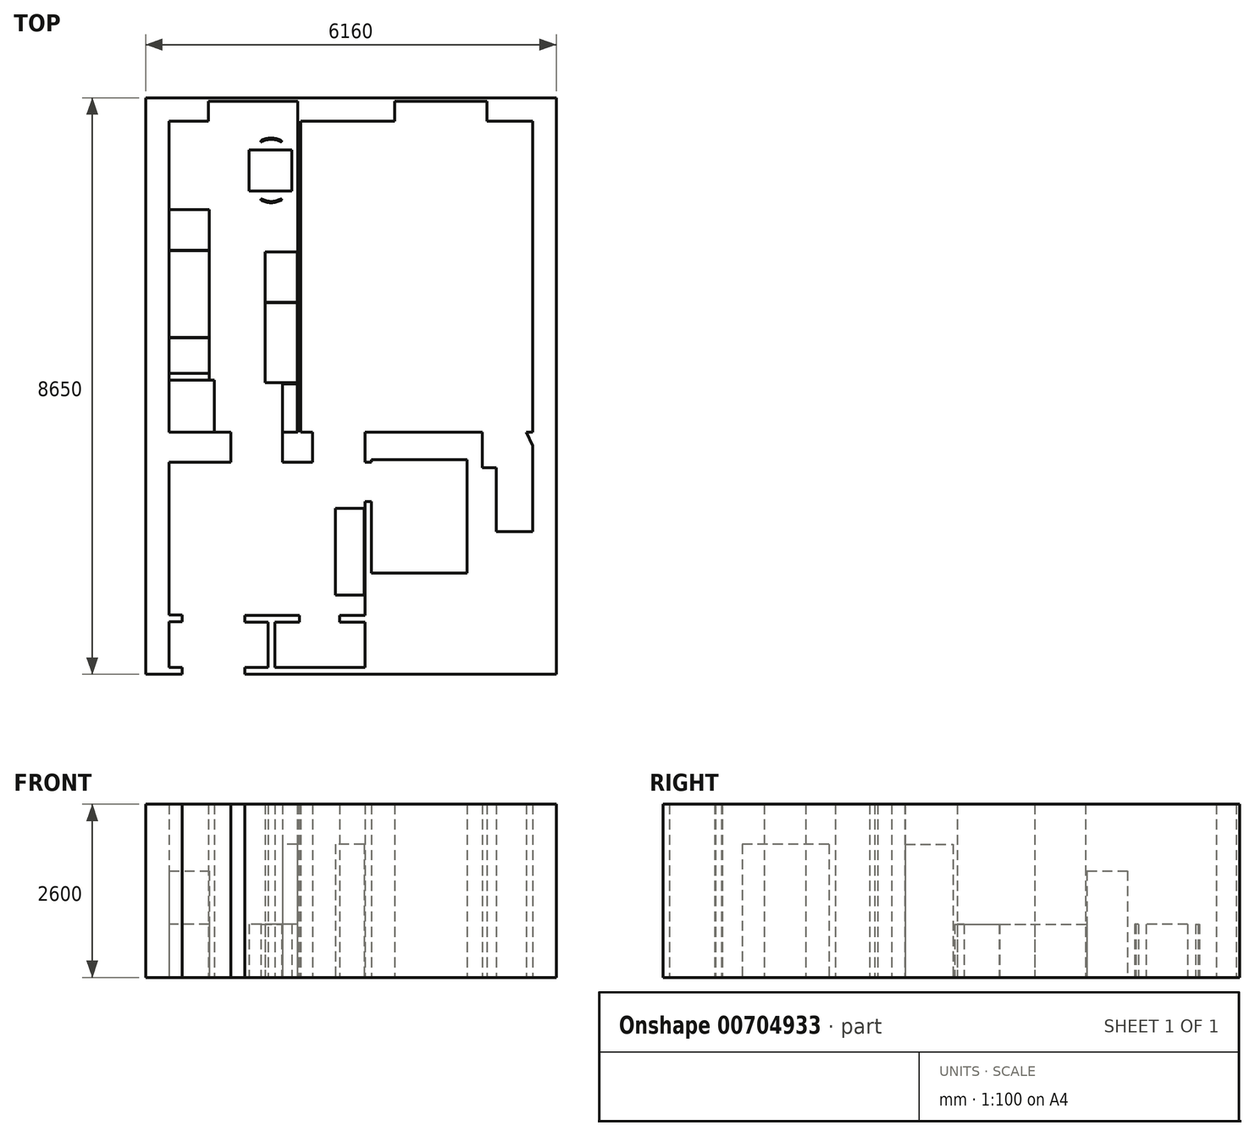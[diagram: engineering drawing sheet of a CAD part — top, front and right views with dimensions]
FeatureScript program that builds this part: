
annotation { "Feature Type Name" : "Feature", "Feature Type Description" : "" }
export const myFeature = defineFeature(function(context is Context, id is Id, definition is map)
    precondition{}
    {
        {
            var Q0;
            Q0=qCreatedBy(makeId("Top.planeOp"),FACE);
            var sketch = newSketch(context, id + "F0", { "sketchPlane" : qUnion([Q0])});
            skLineSegment(sketch, "E0.bottom", {"start": v(0, 5020) * mm, "end": v(-6160, 5020) * mm});
            skLineSegment(sketch, "E0.left", {"start": v(0, 5020) * mm, "end": v(0, -3630) * mm});
            skLineSegment(sketch, "E0.right", {"start": v(-6160, 5020) * mm, "end": v(-6160, -3630) * mm});
            skPoint(sketch, "E0.middle", {"position": v(-3830, 0) * mm});
            skLineSegment(sketch, "E1.bottom", {"start": v(-350, 4670) * mm, "end": v(-1040, 4670) * mm});
            skLineSegment(sketch, "E1.top", {"start": v(-350, 0) * mm, "end": v(-450, 0) * mm});
            skLineSegment(sketch, "E1.left", {"start": v(-350, 4670) * mm, "end": v(-350, 0) * mm});
            skLineSegment(sketch, "E1.right", {"start": v(-3830, 4670) * mm, "end": v(-3830, 0) * mm});
            skLineSegment(sketch, "E2.top", {"start": v(-1040, 4970) * mm, "end": v(-2420, 4970) * mm});
            skLineSegment(sketch, "E2.left", {"start": v(-1040, 4670) * mm, "end": v(-1040, 4970) * mm});
            skLineSegment(sketch, "E2.right", {"start": v(-2420, 4670) * mm, "end": v(-2420, 4970) * mm});
            skLineSegment(sketch, "E3.trimOffspring", {"start": v(-2420, 4670) * mm, "end": v(-3830, 4670) * mm});
            skLineSegment(sketch, "E4", {"start": v(-350, -200) * mm, "end": v(-350, -1490) * mm});
            skLineSegment(sketch, "E5", {"start": v(-350, -1490) * mm, "end": v(-900, -1490) * mm});
            skLineSegment(sketch, "E6", {"start": v(-900, -1490) * mm, "end": v(-900, -530) * mm});
            skLineSegment(sketch, "E7", {"start": v(-900, -530) * mm, "end": v(-1110, -530) * mm});
            skLineSegment(sketch, "E8", {"start": v(-1110, -530) * mm, "end": v(-1110, 0) * mm});
            skLineSegment(sketch, "E9", {"start": v(-450, 0) * mm, "end": v(-350, -200) * mm});
            skLineSegment(sketch, "E10.trimOffspring", {"start": v(-1110, 0) * mm, "end": v(-2870, 0) * mm});
            skLineSegment(sketch, "E11", {"start": v(-3655, 0) * mm, "end": v(-3655, -450) * mm});
            skLineSegment(sketch, "E12", {"start": v(-3655, -450) * mm, "end": v(-4105, -450) * mm});
            skLineSegment(sketch, "E13", {"start": v(-4105, -450) * mm, "end": v(-4105, 0) * mm});
            skLineSegment(sketch, "E14", {"start": v(-4105, 0) * mm, "end": v(-3880, 0) * mm});
            skLineSegment(sketch, "E15", {"start": v(-3880, 0) * mm, "end": v(-3880, 4670) * mm});
            skLineSegment(sketch, "E16", {"start": v(-3880, 4670) * mm, "end": v(-3880, 4970) * mm});
            skLineSegment(sketch, "E17", {"start": v(-3880, 4970) * mm, "end": v(-5220, 4970) * mm});
            skLineSegment(sketch, "E18", {"start": v(-5220, 4970) * mm, "end": v(-5220, 4670) * mm});
            skLineSegment(sketch, "E19", {"start": v(-5220, 4670) * mm, "end": v(-5810, 4670) * mm});
            skLineSegment(sketch, "E20", {"start": v(-5810, 4670) * mm, "end": v(-5810, 0) * mm});
            skLineSegment(sketch, "E21", {"start": v(-5810, 0) * mm, "end": v(-4880, 0) * mm});
            skLineSegment(sketch, "E22", {"start": v(-4880, 0) * mm, "end": v(-4880, -450) * mm});
            skLineSegment(sketch, "E23", {"start": v(-4880, -450) * mm, "end": v(-5810, -450) * mm});
            skLineSegment(sketch, "E24", {"start": v(-5810, -450) * mm, "end": v(-5810, -2740) * mm});
            skLineSegment(sketch, "E25", {"start": v(-2870, -450) * mm, "end": v(-2770, -450) * mm});
            skLineSegment(sketch, "E26", {"start": v(-2770, -450) * mm, "end": v(-2770, -410) * mm});
            skLineSegment(sketch, "E27", {"start": v(-2770, -410) * mm, "end": v(-1340, -410) * mm});
            skLineSegment(sketch, "E28", {"start": v(-1340, -410) * mm, "end": v(-1340, -2110) * mm});
            skLineSegment(sketch, "E29.trimOffspring", {"start": v(-3655, 0) * mm, "end": v(-3830, 0) * mm});
            skLineSegment(sketch, "E30", {"start": v(-5810, -2740) * mm, "end": v(-5610, -2740) * mm});
            skLineSegment(sketch, "E31", {"start": v(-5610, -2740) * mm, "end": v(-5610, -2840) * mm});
            skLineSegment(sketch, "E32", {"start": v(-5610, -2840) * mm, "end": v(-5810, -2840) * mm});
            skLineSegment(sketch, "E33", {"start": v(-5810, -2840) * mm, "end": v(-5810, -3530) * mm});
            skLineSegment(sketch, "E34", {"start": v(-5810, -3530) * mm, "end": v(-5610, -3530) * mm});
            skLineSegment(sketch, "E35", {"start": v(-2870, 0) * mm, "end": v(-2870, -450) * mm});
            skLineSegment(sketch, "E36", {"start": v(-1340, -2110) * mm, "end": v(-2770, -2110) * mm});
            skLineSegment(sketch, "E37", {"start": v(-2770, -2110) * mm, "end": v(-2770, -1040) * mm});
            skLineSegment(sketch, "E38", {"start": v(-2770, -1040) * mm, "end": v(-2870, -1040) * mm});
            skLineSegment(sketch, "E39", {"start": v(-2870, -1040) * mm, "end": v(-2870, -2750) * mm});
            skLineSegment(sketch, "E40.bottom", {"start": v(-2880, -1140) * mm, "end": v(-3310, -1140) * mm});
            skLineSegment(sketch, "E40.top", {"start": v(-2880, -2440) * mm, "end": v(-3310, -2440) * mm});
            skLineSegment(sketch, "E40.left", {"start": v(-2880, -1140) * mm, "end": v(-2880, -2440) * mm});
            skLineSegment(sketch, "E40.right", {"start": v(-3310, -1140) * mm, "end": v(-3310, -2440) * mm});
            skLineSegment(sketch, "E41", {"start": v(-2870, -2750) * mm, "end": v(-3250, -2750) * mm});
            skLineSegment(sketch, "E42", {"start": v(-3250, -2750) * mm, "end": v(-3250, -2850) * mm});
            skLineSegment(sketch, "E43", {"start": v(-3250, -2850) * mm, "end": v(-2870, -2850) * mm});
            skLineSegment(sketch, "E44", {"start": v(-2870, -2850) * mm, "end": v(-2870, -3530) * mm});
            skLineSegment(sketch, "E45", {"start": v(-2870, -3530) * mm, "end": v(-4220, -3530) * mm});
            skLineSegment(sketch, "E46", {"start": v(-4220, -3530) * mm, "end": v(-4220, -2850) * mm});
            skLineSegment(sketch, "E47", {"start": v(-4670, -2750) * mm, "end": v(-3850, -2750) * mm});
            skLineSegment(sketch, "E48", {"start": v(-3850, -2750) * mm, "end": v(-3850, -2850) * mm});
            skPoint(sketch, "E48.endSnap0", {"position": v(-3060, -2850) * mm});
            skLineSegment(sketch, "E49", {"start": v(-3850, -2850) * mm, "end": v(-4220, -2850) * mm});
            skLineSegment(sketch, "E50", {"start": v(-4670, -2750) * mm, "end": v(-4670, -2850) * mm});
            skLineSegment(sketch, "E51", {"start": v(-4670, -2850) * mm, "end": v(-4320, -2850) * mm});
            skLineSegment(sketch, "E52", {"start": v(-4320, -2850) * mm, "end": v(-4320, -3530) * mm});
            skLineSegment(sketch, "E53", {"start": v(-5610, -3530) * mm, "end": v(-5610, -3630) * mm});
            skLineSegment(sketch, "E54", {"start": v(-5610, -3630) * mm, "end": v(-5810, -3630) * mm});
            skLineSegment(sketch, "E55", {"start": v(-4320, -3530) * mm, "end": v(-4670, -3530) * mm});
            skLineSegment(sketch, "E56", {"start": v(-4670, -3530) * mm, "end": v(-4670, -3630) * mm});
            skLineSegment(sketch, "E57", {"start": v(-4670, -3630) * mm, "end": v(-4320, -3630) * mm});
            skLineSegment(sketch, "E58", {"start": v(-5810, -3630) * mm, "end": v(-6160, -3630) * mm});
            skLineSegment(sketch, "E59", {"start": v(-4320, -3630) * mm, "end": v(0, -3630) * mm});
            skLineSegment(sketch, "E60.bottom", {"start": v(-3885, 5) * mm, "end": v(-4105, 5) * mm});
            skLineSegment(sketch, "E60.top", {"start": v(-3885, 725) * mm, "end": v(-4105, 725) * mm});
            skLineSegment(sketch, "E60.left", {"start": v(-3885, 5) * mm, "end": v(-3885, 725) * mm});
            skLineSegment(sketch, "E60.right", {"start": v(-4105, 5) * mm, "end": v(-4105, 725) * mm});
            skLineSegment(sketch, "E61.bottom", {"start": v(-3885, 745) * mm, "end": v(-4365, 745) * mm});
            skLineSegment(sketch, "E61.top", {"start": v(-3885, 1945) * mm, "end": v(-4365, 1945) * mm});
            skLineSegment(sketch, "E61.left", {"start": v(-3885, 745) * mm, "end": v(-3885, 1945) * mm});
            skLineSegment(sketch, "E61.right", {"start": v(-4365, 745) * mm, "end": v(-4365, 1945) * mm});
            skLineSegment(sketch, "E62.bottom", {"start": v(-4365, 1950) * mm, "end": v(-3885, 1950) * mm});
            skLineSegment(sketch, "E62.top", {"start": v(-4365, 2710) * mm, "end": v(-3885, 2710) * mm});
            skLineSegment(sketch, "E62.left", {"start": v(-4365, 1950) * mm, "end": v(-4365, 2710) * mm});
            skLineSegment(sketch, "E62.right", {"start": v(-3885, 1950) * mm, "end": v(-3885, 2710) * mm});
            skLineSegment(sketch, "E63.bottom", {"start": v(-5130, 5) * mm, "end": v(-5805, 5) * mm});
            skLineSegment(sketch, "E63.top", {"start": v(-5130, 785) * mm, "end": v(-5805, 785) * mm});
            skLineSegment(sketch, "E63.left", {"start": v(-5130, 5) * mm, "end": v(-5130, 785) * mm});
            skLineSegment(sketch, "E63.right", {"start": v(-5805, 5) * mm, "end": v(-5805, 785) * mm});
            skLineSegment(sketch, "E64.bottom", {"start": v(-5205, 887) * mm, "end": v(-5805, 887) * mm});
            skLineSegment(sketch, "E64.top", {"start": v(-5205, 1418) * mm, "end": v(-5805, 1418) * mm});
            skLineSegment(sketch, "E64.left", {"start": v(-5205, 887) * mm, "end": v(-5205, 1418) * mm});
            skLineSegment(sketch, "E64.right", {"start": v(-5805, 887) * mm, "end": v(-5805, 1418) * mm});
            skLineSegment(sketch, "E65.bottom", {"start": v(-5205, 886) * mm, "end": v(-5805, 886) * mm});
            skLineSegment(sketch, "E65.top", {"start": v(-5205, 786) * mm, "end": v(-5805, 786) * mm});
            skLineSegment(sketch, "E65.left", {"start": v(-5205, 886) * mm, "end": v(-5205, 786) * mm});
            skLineSegment(sketch, "E65.right", {"start": v(-5805, 886) * mm, "end": v(-5805, 786) * mm});
            skLineSegment(sketch, "E66.bottom", {"start": v(-5205, 1423) * mm, "end": v(-5805, 1423) * mm});
            skLineSegment(sketch, "E66.top", {"start": v(-5205, 2727.47) * mm, "end": v(-5805, 2727.47) * mm});
            skLineSegment(sketch, "E66.left", {"start": v(-5205, 1423) * mm, "end": v(-5205, 2727.47) * mm});
            skLineSegment(sketch, "E66.right", {"start": v(-5805, 1423) * mm, "end": v(-5805, 2727.47) * mm});
            skLineSegment(sketch, "E67.bottom", {"start": v(-5805, 2732.47) * mm, "end": v(-5205, 2732.47) * mm});
            skLineSegment(sketch, "E67.top", {"start": v(-5805, 3339.8) * mm, "end": v(-5205, 3339.8) * mm});
            skLineSegment(sketch, "E67.left", {"start": v(-5805, 2732.47) * mm, "end": v(-5805, 3339.8) * mm});
            skLineSegment(sketch, "E67.right", {"start": v(-5205, 2732.47) * mm, "end": v(-5205, 3339.8) * mm});
            skLineSegment(sketch, "E68.bottom", {"start": v(-3967.42, 4241.29) * mm, "end": v(-4610.31, 4241.29) * mm});
            skLineSegment(sketch, "E68.top", {"start": v(-3967.42, 3621.1) * mm, "end": v(-4610.31, 3621.1) * mm});
            skLineSegment(sketch, "E68.left", {"start": v(-3967.42, 4241.29) * mm, "end": v(-3967.42, 3621.1) * mm});
            skLineSegment(sketch, "E68.right", {"start": v(-4610.31, 4241.29) * mm, "end": v(-4610.31, 3621.1) * mm});
            skArc(sketch, "E69", {"start": v(-4421.58, 3492.54) * mm, "mid": v(-4275.23, 3455.4) * mm, "end": v(-4128.88, 3492.54) * mm});
            skArc(sketch, "E70.0.startCap", {"start": v(-4426.35, 3483.75) * mm, "mid": v(-4430.37, 3497.3) * mm, "end": v(-4416.81, 3501.33) * mm});
            skArc(sketch, "E70.0.endCap", {"start": v(-4133.65, 3501.33) * mm, "mid": v(-4120.1, 3497.3) * mm, "end": v(-4124.11, 3483.75) * mm});
            skArc(sketch, "E70.0.left", {"start": v(-4416.81, 3501.33) * mm, "mid": v(-4275.23, 3465.4) * mm, "end": v(-4133.65, 3501.33) * mm});
            skArc(sketch, "E70.0.right", {"start": v(-4426.35, 3483.75) * mm, "mid": v(-4275.23, 3445.4) * mm, "end": v(-4124.11, 3483.75) * mm});
            skLineSegment(sketch, "E71", {"start": v(-4610.31, 3931.2) * mm, "end": v(-3967.42, 3931.2) * mm, "construction": true});
            skArc(sketch, "E72.MirrorCS", {"start": v(-4133.65, 4361.05) * mm, "mid": v(-4120.1, 4365.07) * mm, "end": v(-4124.11, 4378.63) * mm});
            skArc(sketch, "E73.MirrorCS", {"start": v(-4426.35, 4378.63) * mm, "mid": v(-4430.37, 4365.07) * mm, "end": v(-4416.81, 4361.05) * mm});
            skArc(sketch, "E74.MirrorCS", {"start": v(-4421.58, 4369.84) * mm, "mid": v(-4275.23, 4406.97) * mm, "end": v(-4128.88, 4369.84) * mm});
            skArc(sketch, "E75.MirrorCS", {"start": v(-4416.81, 4361.05) * mm, "mid": v(-4275.23, 4396.97) * mm, "end": v(-4133.65, 4361.05) * mm});
            skArc(sketch, "E76.MirrorCS", {"start": v(-4426.35, 4378.63) * mm, "mid": v(-4275.23, 4416.97) * mm, "end": v(-4124.11, 4378.63) * mm});
            skSolve(sketch);
        }
        {
            var Q0;
            Q0 = qSketchRegion(id + "F0", true);
            extrude(context, id + "F1", {"entities" : qUnion([Q0]), "depth" : 800 * mm, "offsetDistance" : 25 * mm});
        }
        {
            var Q0;
            Q0=makeQuery(id+"F1.opExtrude","CAP_FACE",FACE,{"disambiguationData":[OSD([sQuery(id+"F0.wireOp",EDGE,"E40.bottom"),sQuery(id+"F0.wireOp",EDGE,"E40.top"),sQuery(id+"F0.wireOp",EDGE,"E40.left"),sQuery(id+"F0.wireOp",EDGE,"E40.right")])],"isStart":false});
            var Q1;
            Q1=makeQuery(id+"F1.opExtrude","CAP_FACE",FACE,{"disambiguationData":[OSD([sQuery(id+"F0.wireOp",EDGE,"E60.bottom"),sQuery(id+"F0.wireOp",EDGE,"E60.top"),sQuery(id+"F0.wireOp",EDGE,"E60.left"),sQuery(id+"F0.wireOp",EDGE,"E60.right")])],"isStart":false});
            extrude(context, id + "F2", {"entities" : qUnion([Q0, Q1]), "operationType" : NewBodyOperationType.ADD, "depth" : 1200 * mm, "offsetDistance" : 25 * mm});
        }
        {
            var Q0;
            Q0=makeQuery(id+"F1.opExtrude","CAP_FACE",FACE,{"disambiguationData":[OSD([sQuery(id+"F0.wireOp",EDGE,"E67.bottom"),sQuery(id+"F0.wireOp",EDGE,"E67.top"),sQuery(id+"F0.wireOp",EDGE,"E67.left"),sQuery(id+"F0.wireOp",EDGE,"E67.right")])],"isStart":false});
            extrude(context, id + "F3", {"entities" : qUnion([Q0]), "operationType" : NewBodyOperationType.ADD, "depth" : 800 * mm, "offsetDistance" : 25 * mm});
        }
        {
            var Q0;
            Q0=makeQuery(id+"F1.opExtrude","CAP_FACE",FACE,{"disambiguationData":[OSD([sQuery(id+"F0.wireOp",EDGE,"E0.bottom"),sQuery(id+"F0.wireOp",EDGE,"E0.left"),sQuery(id+"F0.wireOp",EDGE,"E0.right"),sQuery(id+"F0.wireOp",EDGE,"E1.bottom"),sQuery(id+"F0.wireOp",EDGE,"E1.top"),sQuery(id+"F0.wireOp",EDGE,"E1.left"),sQuery(id+"F0.wireOp",EDGE,"E1.right"),sQuery(id+"F0.wireOp",EDGE,"E2.top"),sQuery(id+"F0.wireOp",EDGE,"E2.left"),sQuery(id+"F0.wireOp",EDGE,"E2.right"),sQuery(id+"F0.wireOp",EDGE,"E3.trimOffspring"),sQuery(id+"F0.wireOp",EDGE,"E4"),sQuery(id+"F0.wireOp",EDGE,"E5"),sQuery(id+"F0.wireOp",EDGE,"E6"),sQuery(id+"F0.wireOp",EDGE,"E7"),sQuery(id+"F0.wireOp",EDGE,"E8"),sQuery(id+"F0.wireOp",EDGE,"E9"),sQuery(id+"F0.wireOp",EDGE,"E10.trimOffspring"),sQuery(id+"F0.wireOp",EDGE,"E11"),sQuery(id+"F0.wireOp",EDGE,"E12"),sQuery(id+"F0.wireOp",EDGE,"E13"),sQuery(id+"F0.wireOp",EDGE,"E14"),sQuery(id+"F0.wireOp",EDGE,"E15"),sQuery(id+"F0.wireOp",EDGE,"E16"),sQuery(id+"F0.wireOp",EDGE,"E17"),sQuery(id+"F0.wireOp",EDGE,"E18"),sQuery(id+"F0.wireOp",EDGE,"E19"),sQuery(id+"F0.wireOp",EDGE,"E20"),sQuery(id+"F0.wireOp",EDGE,"E21"),sQuery(id+"F0.wireOp",EDGE,"E22"),sQuery(id+"F0.wireOp",EDGE,"E23"),sQuery(id+"F0.wireOp",EDGE,"E24"),sQuery(id+"F0.wireOp",EDGE,"E25"),sQuery(id+"F0.wireOp",EDGE,"E26"),sQuery(id+"F0.wireOp",EDGE,"E27"),sQuery(id+"F0.wireOp",EDGE,"E28"),sQuery(id+"F0.wireOp",EDGE,"E29.trimOffspring"),sQuery(id+"F0.wireOp",EDGE,"E30"),sQuery(id+"F0.wireOp",EDGE,"E31"),sQuery(id+"F0.wireOp",EDGE,"E32"),sQuery(id+"F0.wireOp",EDGE,"E33"),sQuery(id+"F0.wireOp",EDGE,"E34"),sQuery(id+"F0.wireOp",EDGE,"E35"),sQuery(id+"F0.wireOp",EDGE,"E36"),sQuery(id+"F0.wireOp",EDGE,"E37"),sQuery(id+"F0.wireOp",EDGE,"E38"),sQuery(id+"F0.wireOp",EDGE,"E39"),sQuery(id+"F0.wireOp",EDGE,"E41"),sQuery(id+"F0.wireOp",EDGE,"E42"),sQuery(id+"F0.wireOp",EDGE,"E43"),sQuery(id+"F0.wireOp",EDGE,"E44"),sQuery(id+"F0.wireOp",EDGE,"E45"),sQuery(id+"F0.wireOp",EDGE,"E46"),sQuery(id+"F0.wireOp",EDGE,"E47"),sQuery(id+"F0.wireOp",EDGE,"E48"),sQuery(id+"F0.wireOp",EDGE,"E49"),sQuery(id+"F0.wireOp",EDGE,"E50"),sQuery(id+"F0.wireOp",EDGE,"E51"),sQuery(id+"F0.wireOp",EDGE,"E52"),sQuery(id+"F0.wireOp",EDGE,"E53"),sQuery(id+"F0.wireOp",EDGE,"E54"),sQuery(id+"F0.wireOp",EDGE,"E55"),sQuery(id+"F0.wireOp",EDGE,"E56"),sQuery(id+"F0.wireOp",EDGE,"E57"),sQuery(id+"F0.wireOp",EDGE,"E58"),sQuery(id+"F0.wireOp",EDGE,"E59")])],"isStart":false});
            var Q1;
            Q1=makeQuery(id+"F1.opExtrude","CAP_FACE",FACE,{"disambiguationData":[OSD([sQuery(id+"F0.wireOp",EDGE,"E63.bottom"),sQuery(id+"F0.wireOp",EDGE,"E63.top"),sQuery(id+"F0.wireOp",EDGE,"E63.left"),sQuery(id+"F0.wireOp",EDGE,"E63.right")])],"isStart":false});
            var Q2;
            Q2=makeQuery(id+"F1.opExtrude","CAP_FACE",FACE,{"disambiguationData":[OSD([sQuery(id+"F0.wireOp",EDGE,"E62.bottom"),sQuery(id+"F0.wireOp",EDGE,"E62.top"),sQuery(id+"F0.wireOp",EDGE,"E62.left"),sQuery(id+"F0.wireOp",EDGE,"E62.right")])],"isStart":false});
            extrude(context, id + "F4", {"entities" : qUnion([Q0, Q1, Q2]), "operationType" : NewBodyOperationType.ADD, "depth" : 1800 * mm, "offsetDistance" : 25 * mm});
        }
    });
